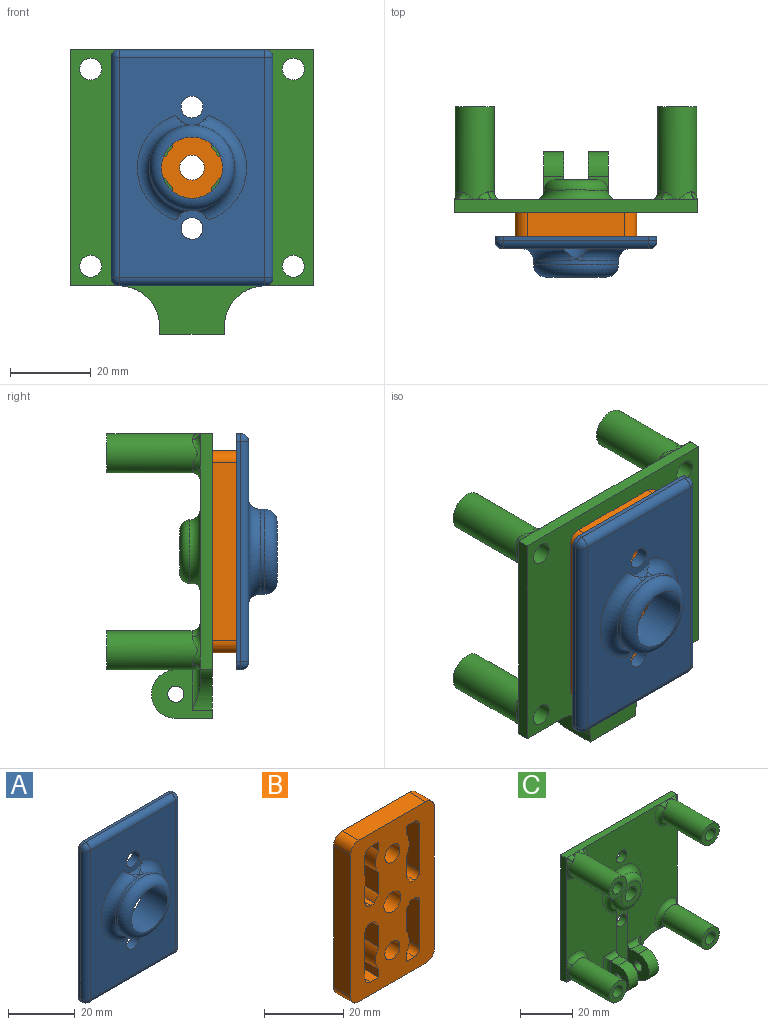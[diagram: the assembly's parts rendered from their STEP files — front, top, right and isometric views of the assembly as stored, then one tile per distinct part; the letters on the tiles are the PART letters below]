
ASSEMBLY  parts=3 mates=2
PART A: 29 faces, bbox 40x10x58.4 mm
  f0: bspline ~4.4x3.18mm, area 3.2mm2, adj f1,f2,f13,f28
  f1: torus R=13.5mm, axis (0,-1,0), area 149.2mm2, adj f0,f3,f11,f13,f27,f28
  f2: torus R=13.5mm, axis (0,-1,0), area 149.2mm2, adj f0,f3,f11,f13,f27,f28
  f3: bspline ~4.4x3.18mm, area 3.2mm2, adj f1,f2,f13,f27
  f4: plane 36x1mm, normal (0,0,1), area 36mm2, adj f12,f17,f23,f26
  f5: plane 54.36x1mm, normal (-1,0,0), area 54.4mm2, adj f12,f20,f24,f26
  f6: plane 36x1mm, normal (0,0,-1), area 36mm2, adj f12,f15,f19,f20
  f7: plane 54.36x1mm, normal (1,0,0), area 54.4mm2, adj f12,f15,f17,f18
  f8: cylinder r=2.7mm len=5.4mm, axis (0,1,0), area 50.9mm2, adj f11,f12
  f9: cylinder r=2.7mm len=5.4mm, axis (0,1,0), area 50.9mm2, adj f11,f12
  f10: cylinder r=7.55mm len=15.1mm, axis (0,1,0), area 474.4mm2, adj f12,f14
  f11: plane 54.36x36mm, normal (0,-1,0), area 1371.7mm2, adj f1,f2,f8,f9,f18,f19,f23,f24
  f12: plane 58.36x40mm, normal (0,1,0), area 2106mm2, adj f4,f5,f6,f7,f8,f9,f10,f15
  f13: cylinder r=10.5mm len=21mm, axis (0,1,0), area 66mm2, adj f0,f1,f2,f3,f14
  f14: torus R=7.5mm, axis (0,-1,0), area 276.3mm2, adj f10,f13
  f15: cylinder r=2mm len=2mm, axis (0,-1,0), area 3.1mm2, adj f6,f7,f12,f16
  f16: sphere r=2mm, area 6.3mm2, adj f15,f18,f19
  f17: cylinder r=2mm len=2mm, axis (0,1,0), area 3.1mm2, adj f4,f7,f12,f21
  f18: cylinder r=2mm len=54.36mm, axis (0,0,-1), area 170.8mm2, adj f7,f11,f16,f21
  f19: cylinder r=2mm len=36mm, axis (-1,0,0), area 113.1mm2, adj f6,f11,f16,f22
  f20: cylinder r=2mm len=2mm, axis (0,1,0), area 3.1mm2, adj f5,f6,f12,f22
  f21: sphere r=2mm, area 6.3mm2, adj f17,f18,f23
  f22: sphere r=2mm, area 6.3mm2, adj f19,f20,f24
  f23: cylinder r=2mm len=36mm, axis (1,0,0), area 113.1mm2, adj f4,f11,f21,f25
  f24: cylinder r=2mm len=54.36mm, axis (0,0,1), area 170.8mm2, adj f5,f11,f22,f25
  f25: sphere r=2mm, area 6.3mm2, adj f23,f24,f26
  f26: cylinder r=2mm len=2mm, axis (0,-1,0), area 3.1mm2, adj f4,f5,f12,f25
  f27: cylinder r=4.48mm len=7.91mm, axis (0,1,0), area 8.8mm2, adj f1,f2,f3,f11
  f28: cylinder r=4.48mm len=7.92mm, axis (0,1,0), area 8.8mm2, adj f0,f1,f2,f11
PART B: 49 faces, bbox 30x6x50 mm
  f0: plane 24x6mm, normal (0,0,1), area 144mm2, adj f1,f46,f47,f48
  f1: cylinder r=3mm len=6mm, axis (0,1,0), area 28.3mm2, adj f0,f2,f47,f48
  f2: plane 44x6mm, normal (-1,0,0), area 264mm2, adj f1,f3,f47,f48
  f3: cylinder r=3mm len=6mm, axis (0,1,0), area 28.3mm2, adj f2,f4,f47,f48
  f4: plane 24x6mm, normal (0,0,-1), area 144mm2, adj f3,f5,f47,f48
  f5: cylinder r=3mm len=6mm, axis (0,1,0), area 28.3mm2, adj f4,f6,f47,f48
  f6: plane 44x6mm, normal (1,0,0), area 264mm2, adj f5,f46,f47,f48
  f7: plane 6x2.55mm, normal (1,0,0), area 15.3mm2, adj f8,f39,f47,f48
  f8: plane 6x2.91mm, normal (0,0,-1), area 17.5mm2, adj f7,f9,f47,f48
  f9: cylinder r=2mm len=6mm, axis (0,1,0), area 18.8mm2, adj f8,f10,f47,f48
  f10: plane 14.25x6mm, normal (-1,0,0), area 85.5mm2, adj f9,f11,f47,f48
  f11: cylinder r=2mm len=6mm, axis (0,1,0), area 18.8mm2, adj f10,f12,f47,f48
  f12: plane 6x1.39mm, normal (0,0,1), area 8.3mm2, adj f11,f13,f47,f48
  f13: cylinder r=7mm len=6mm, axis (0,1,0), area 16.3mm2, adj f12,f14,f47,f48
  f14: plane 6.57x6mm, normal (1,0,0), area 39.4mm2, adj f13,f39,f47,f48
  f15: cylinder r=6mm len=6.89mm, axis (0,1,0), area 44.1mm2, adj f16,f40,f47,f48
  f16: plane 6.57x6mm, normal (1,0,0), area 39.4mm2, adj f15,f17,f47,f48
  f17: cylinder r=7mm len=6mm, axis (0,1,0), area 16.3mm2, adj f16,f18,f47,f48
  f18: plane 6x1.39mm, normal (0,0,-1), area 8.3mm2, adj f17,f19,f47,f48
  f19: cylinder r=2mm len=6mm, axis (0,1,0), area 18.8mm2, adj f18,f20,f47,f48
  f20: plane 14.22x6mm, normal (-1,0,0), area 85.3mm2, adj f19,f21,f47,f48
  f21: cylinder r=2mm len=6mm, axis (0,1,0), area 18.8mm2, adj f20,f22,f47,f48
  f22: plane 6x2.91mm, normal (0,0,1), area 17.5mm2, adj f21,f40,f47,f48
  f23: cylinder r=7mm len=6mm, axis (0,1,0), area 16.3mm2, adj f24,f43,f47,f48
  f24: plane 6.57x6mm, normal (-1,0,0), area 39.4mm2, adj f23,f25,f47,f48
  f25: cylinder r=6mm len=6.89mm, axis (0,1,0), area 44.1mm2, adj f24,f26,f47,f48
  f26: plane 6x2.53mm, normal (-1,0,0), area 15.2mm2, adj f25,f27,f47,f48
  f27: plane 6x2.91mm, normal (0,0,1), area 17.5mm2, adj f26,f28,f47,f48
  f28: cylinder r=2mm len=6mm, axis (0,1,0), area 18.8mm2, adj f27,f29,f47,f48
  f29: plane 14.22x6mm, normal (1,0,0), area 85.3mm2, adj f28,f30,f47,f48
  f30: cylinder r=2mm len=6mm, axis (0,1,0), area 18.8mm2, adj f29,f43,f47,f48
  f31: plane 6x2.91mm, normal (0,0,-1), area 17.5mm2, adj f32,f44,f47,f48
  f32: plane 6x2.55mm, normal (-1,0,0), area 15.3mm2, adj f31,f33,f47,f48
  f33: cylinder r=6mm len=6.89mm, axis (0,1,0), area 44.1mm2, adj f32,f34,f47,f48
  f34: plane 6.57x6mm, normal (-1,0,0), area 39.4mm2, adj f33,f35,f47,f48
  f35: cylinder r=7mm len=6mm, axis (0,1,0), area 16.3mm2, adj f34,f36,f47,f48
  f36: plane 6x1.39mm, normal (0,0,1), area 8.3mm2, adj f35,f37,f47,f48
  f37: cylinder r=2mm len=6mm, axis (0,1,0), area 18.8mm2, adj f36,f38,f47,f48
  f38: plane 14.25x6mm, normal (1,0,0), area 85.5mm2, adj f37,f44,f47,f48
  f39: cylinder r=6mm len=6.89mm, axis (0,1,0), area 44.1mm2, adj f7,f14,f47,f48
  f40: plane 6x2.53mm, normal (1,0,0), area 15.2mm2, adj f15,f22,f47,f48
  f41: cylinder r=3.05mm len=6.1mm, axis (0,1,0), area 115mm2, adj f47,f48
  f42: cylinder r=2.7mm len=6mm, axis (0,1,0), area 101.8mm2, adj f47,f48
  f43: plane 6x1.39mm, normal (0,0,-1), area 8.3mm2, adj f23,f30,f47,f48
  f44: cylinder r=2mm len=6mm, axis (0,1,0), area 18.8mm2, adj f31,f38,f47,f48
  f45: cylinder r=2.7mm len=6mm, axis (0,1,0), area 101.8mm2, adj f47,f48
  f46: cylinder r=3mm len=6mm, axis (0,1,0), area 28.3mm2, adj f0,f6,f47,f48
  f47: plane 50x30mm, normal (0,-1,0), area 1094.1mm2, adj f0,f1,f2,f3,f4,f5,f6,f7
  f48: plane 50x30mm, normal (0,1,0), area 1094.1mm2, adj f0,f1,f2,f3,f4,f5,f6,f7
PART C: 68 faces, bbox 63.4x26.3x72.2 mm
  f0: plane 34.16x12.27mm, normal (-1,0,0), area 118.9mm2, adj f2,f8,f9,f10,f15,f31,f62,f64
  f1: plane 34.16x12.27mm, normal (1,0,0), area 118.9mm2, adj f2,f15,f26,f27,f28,f31,f61,f64
  f2: plane 62.36x60mm, normal (0,-1,0), area 2533.9mm2, adj f0,f1,f11,f12,f13,f17,f19,f23
  f3: plane 0.14x0.13mm, normal (0,-1,0), area 0mm2, adj f12,f13,f48
  f4: plane 0.14x0.13mm, normal (0,-1,0), area 0mm2, adj f11,f23,f53
  f5: plane 0.14x0.13mm, normal (0,-1,0), area 0mm2, adj f17,f23,f41
  f6: plane 0.14x0.13mm, normal (0,-1,0), area 0mm2, adj f11,f12,f56
  f7: cylinder r=3.1mm len=8mm, axis (0,1,0), area 155.8mm2, adj f25,f65
  f8: plane 5x4mm, normal (0,0,1), area 20mm2, adj f0,f9,f16,f62
  f9: cylinder r=6mm len=12mm, axis (-1,0,0), area 94.2mm2, adj f0,f8,f15,f16
  f10: cylinder r=2mm len=5mm, axis (-1,0,0), area 62.8mm2, adj f0,f16
  f11: plane 60x3mm, normal (0,0,1), area 180mm2, adj f2,f4,f6,f12,f23,f25,f50,f54
  f12: plane 58.69x3.33mm, normal (-1,0,0), area 175.1mm2, adj f2,f3,f6,f11,f13,f25,f47,f57
  f13: plane 12x3mm, normal (0,0,-1), area 36mm2, adj f2,f3,f12,f25,f29,f45,f49
  f14: plane 15x12mm, normal (-1,0,0), area 102mm2, adj f15,f25,f26,f27,f28,f29,f60
  f15: plane 16x9mm, normal (0,0,-1), area 107.9mm2, adj f0,f1,f9,f14,f16,f25,f27,f31
  f16: plane 15x12mm, normal (1,0,0), area 102mm2, adj f8,f9,f10,f15,f25,f30,f63
  f17: plane 12x3mm, normal (0,0,-1), area 36mm2, adj f2,f5,f23,f25,f30,f40,f44
  f18: cylinder r=2.7mm len=5.4mm, axis (0,1,0), area 50.6mm2, adj f25,f31
  f19: cylinder r=2.7mm len=5.4mm, axis (0,1,0), area 50.9mm2, adj f2,f25
  f20: cylinder r=2.7mm len=26mm, axis (0,1,0), area 441.1mm2, adj f25,f39
  f21: cylinder r=2.7mm len=26mm, axis (0,1,0), area 441.1mm2, adj f25,f37
  f22: cylinder r=2.7mm len=26mm, axis (0,1,0), area 441.1mm2, adj f25,f35
  f23: plane 58.69x3.33mm, normal (1,0,0), area 175.1mm2, adj f2,f4,f5,f11,f17,f25,f42,f52
  f24: cylinder r=2.7mm len=26mm, axis (0,1,0), area 441.1mm2, adj f25,f33
  f25: plane 70.36x60mm, normal (0,1,0), area 3568.8mm2, adj f7,f11,f12,f13,f14,f15,f16,f17
  f26: plane 5x4mm, normal (0,0,1), area 20mm2, adj f1,f14,f27,f61
  f27: cylinder r=6mm len=12mm, axis (-1,0,0), area 94.2mm2, adj f1,f14,f15,f26
  f28: cylinder r=2mm len=5mm, axis (-1,0,0), area 62.8mm2, adj f1,f14
  f29: cylinder r=10mm len=10mm, axis (0,1,0), area 53.6mm2, adj f2,f13,f14,f25,f60
  f30: cylinder r=10mm len=10mm, axis (0,-1,0), area 53.6mm2, adj f2,f16,f17,f25,f63
  f31: plane 33.9x6mm, normal (0,-1,0), area 178.1mm2, adj f0,f1,f15,f18,f64
  f32: cylinder r=4.83mm len=23mm, axis (0,1,0), area 647mm2, adj f33,f55,f56,f57,f58,f59
  f33: plane 9.65x9.65mm, normal (0,-1,0), area 50.3mm2, adj f24,f32
  f34: cylinder r=4.83mm len=23mm, axis (0,1,0), area 647mm2, adj f35,f50,f51,f52,f53,f54
  f35: plane 9.65x9.65mm, normal (0,-1,0), area 50.3mm2, adj f22,f34
  f36: cylinder r=4.83mm len=23mm, axis (0,1,0), area 647mm2, adj f37,f45,f46,f47,f48,f49
  f37: plane 9.65x9.65mm, normal (0,-1,0), area 50.3mm2, adj f21,f36
  f38: cylinder r=4.83mm len=23mm, axis (0,1,0), area 647mm2, adj f39,f40,f41,f42,f43,f44
  f39: plane 9.65x9.65mm, normal (0,-1,0), area 50.3mm2, adj f20,f38
  f40: bspline ~4.97x2.09mm, area 5.4mm2, adj f17,f38,f41
  f41: torus R=6.83mm, axis (0,-1,0), area 0.5mm2, adj f5,f38,f40,f42
  f42: bspline ~9.77x2.15mm, area 13.1mm2, adj f23,f38,f41,f43
  f43: torus R=6.83mm, axis (0,-1,0), area 55.3mm2, adj f2,f38,f42,f44
  f44: bspline ~4.97x2.09mm, area 5.4mm2, adj f17,f38,f43
  f45: bspline ~4.97x2.09mm, area 5.4mm2, adj f13,f36,f46
  f46: torus R=6.83mm, axis (0,-1,0), area 55.3mm2, adj f2,f36,f45,f47
  f47: bspline ~9.77x2.15mm, area 13.1mm2, adj f12,f36,f46,f48
  f48: torus R=6.83mm, axis (0,-1,0), area 0.5mm2, adj f3,f36,f47,f49
  f49: bspline ~4.97x2.09mm, area 5.4mm2, adj f13,f36,f48
  f50: bspline ~4.97x2.09mm, area 5.4mm2, adj f11,f34,f51
  f51: torus R=6.83mm, axis (0,-1,0), area 55.3mm2, adj f2,f34,f50,f52
  f52: bspline ~9.77x2.15mm, area 13.1mm2, adj f23,f34,f51,f53
  f53: torus R=6.83mm, axis (0,-1,0), area 0.5mm2, adj f4,f34,f52,f54
  f54: bspline ~4.97x2.09mm, area 5.4mm2, adj f11,f34,f53
  f55: bspline ~4.97x2.09mm, area 5.4mm2, adj f11,f32,f56
  f56: torus R=6.83mm, axis (0,-1,0), area 0.5mm2, adj f6,f32,f55,f57
  f57: bspline ~9.77x2.15mm, area 13.1mm2, adj f12,f32,f56,f58
  f58: torus R=6.83mm, axis (0,-1,0), area 55.3mm2, adj f2,f32,f57,f59
  f59: bspline ~4.97x2.09mm, area 5.4mm2, adj f11,f32,f58
  f60: cylinder r=2mm len=12mm, axis (0,0,1), area 25.1mm2, adj f2,f14,f29,f61
  f61: cylinder r=2mm len=7mm, axis (-1,0,0), area 18.8mm2, adj f1,f2,f26,f60
  f62: cylinder r=2mm len=7mm, axis (-1,0,0), area 18.8mm2, adj f0,f2,f8,f63
  f63: cylinder r=2mm len=12mm, axis (0,0,1), area 25.1mm2, adj f2,f16,f30,f62
  f64: cylinder r=7.87mm len=6mm, axis (0,1,0), area 15.5mm2, adj f0,f1,f31,f66
  f65: plane 10.74x10.74mm, normal (0,-1,0), area 60.5mm2, adj f7,f66
  f66: torus R=5.37mm, axis (0,-1,0), area 171.8mm2, adj f64,f65,f67
  f67: torus R=10.37mm, axis (0,-1,0), area 193.2mm2, adj f0,f1,f2,f66
PLACE A t=(-46.58,-42.51,1.95)mm
PLACE B t=(-46.58,-36.51,1.95)mm
PLACE C rot(axis=(0,0,1),180deg) t=(-46.58,-36.51,1.95)mm
MATE fastened A.f10 <-> B.f41  axis (0,1,0) through (-46.58,-42.51,1.95)mm
MATE fastened C.f7 <-> B.f41  axis (0,-1,0) through (-46.58,-36.51,1.95)mm
